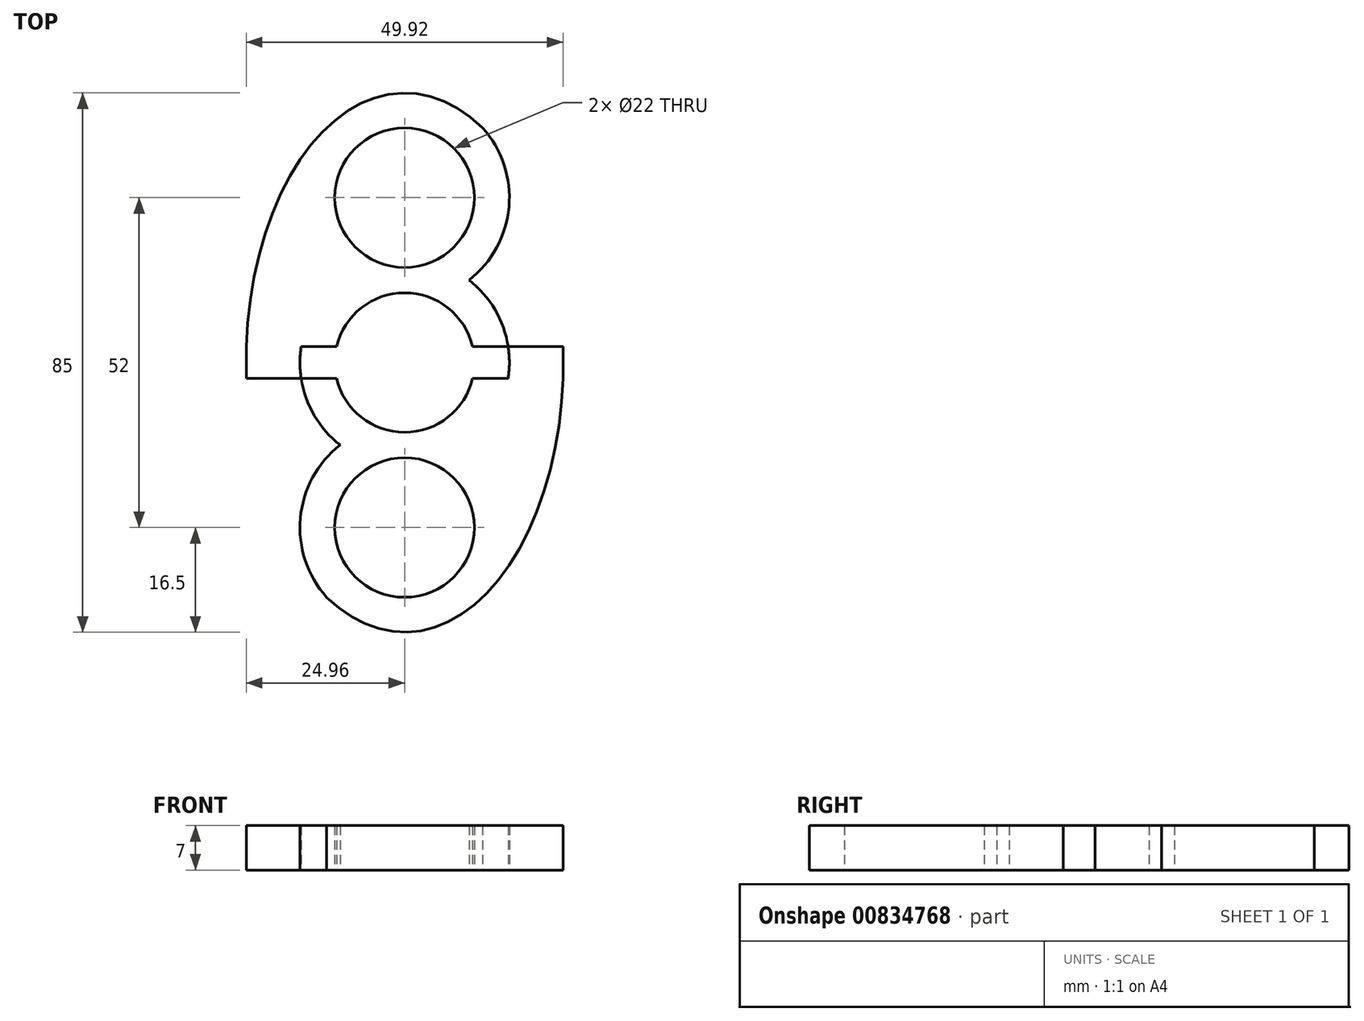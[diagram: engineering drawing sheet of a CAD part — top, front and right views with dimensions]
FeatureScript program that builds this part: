
annotation { "Feature Type Name" : "Feature", "Feature Type Description" : "" }
export const myFeature = defineFeature(function(context is Context, id is Id, definition is map)
    precondition{}
    {
        {
            var Q0;
            Q0=qCreatedBy(makeId("Top.planeOp"),FACE);
            var sketch = newSketch(context, id + "F0", { "sketchPlane" : qUnion([Q0])});
            skEllipse(sketch, "E0", {"center": v(0, 0) * mm, "majorRadius": 42.5 * mm, "minorRadius": 25 * mm, "majorAxis": v(0, 1)});
            skLineSegment(sketch, "E1", {"start": v(0, 0) * mm, "end": v(0, 26) * mm});
            skLineSegment(sketch, "E2.MirrorCS", {"start": v(0, 0) * mm, "end": v(0, -26) * mm});
            skCircle(sketch, "E3", {"center": v(0, 26) * mm, "radius": 11 * mm});
            skCircle(sketch, "E4", {"center": v(0, 0) * mm, "radius": 11 * mm});
            skCircle(sketch, "E5", {"center": v(0, -26) * mm, "radius": 11 * mm});
            skFitSpline(sketch, "E6.0", {"points": [v(1.55, 36.91) * mm, v(0, 37.04) * mm, v(-1.55, 36.91) * mm, v(-3.12, 36.52) * mm, v(-4.74, 35.83) * mm, v(-6.4, 34.82) * mm, v(-8.08, 33.48) * mm, v(-9.75, 31.78) * mm, v(-11.12, 30.07) * mm, v(-12.17, 28.52) * mm, v(-12.94, 27.28) * mm, v(-13.68, 25.95) * mm, v(-14.63, 24.1) * mm, v(-15.7, 21.6) * mm, v(-16.84, 18.4) * mm, v(-17.79, 14.99) * mm, v(-18.54, 11.41) * mm, v(-19.09, 7.7) * mm, v(-19.37, 4.53) * mm, v(-19.48, 1.95) * mm, v(-19.5, 0) * mm, v(-19.48, -1.95) * mm, v(-19.37, -4.53) * mm, v(-19.09, -7.7) * mm, v(-18.54, -11.41) * mm, v(-17.79, -14.99) * mm, v(-16.84, -18.4) * mm, v(-15.7, -21.6) * mm, v(-14.63, -24.1) * mm, v(-13.68, -25.95) * mm, v(-12.94, -27.28) * mm, v(-12.17, -28.52) * mm, v(-11.12, -30.07) * mm, v(-9.75, -31.78) * mm, v(-8.08, -33.48) * mm, v(-6.4, -34.82) * mm, v(-4.74, -35.83) * mm, v(-3.12, -36.52) * mm, v(-1.55, -36.91) * mm, v(0, -37.04) * mm, v(1.55, -36.91) * mm, v(3.12, -36.52) * mm, v(4.74, -35.83) * mm, v(6.4, -34.82) * mm, v(8.08, -33.48) * mm, v(9.75, -31.78) * mm, v(11.12, -30.07) * mm, v(12.17, -28.52) * mm, v(12.94, -27.28) * mm, v(13.68, -25.95) * mm, v(14.63, -24.1) * mm, v(15.7, -21.6) * mm, v(16.84, -18.4) * mm, v(17.79, -14.99) * mm, v(18.54, -11.41) * mm, v(19.09, -7.7) * mm, v(19.37, -4.53) * mm, v(19.48, -1.95) * mm, v(19.5, 0) * mm, v(19.48, 1.95) * mm, v(19.37, 4.53) * mm, v(19.09, 7.7) * mm, v(18.54, 11.41) * mm, v(17.79, 14.99) * mm, v(16.84, 18.4) * mm, v(15.7, 21.6) * mm, v(14.63, 24.1) * mm, v(13.68, 25.95) * mm, v(12.94, 27.28) * mm, v(12.17, 28.52) * mm, v(11.12, 30.07) * mm, v(9.75, 31.78) * mm, v(8.08, 33.48) * mm, v(6.4, 34.82) * mm, v(4.74, 35.83) * mm, v(3.12, 36.52) * mm, v(1.55, 36.91) * mm, v(0, 37.04) * mm, v(-1.55, 36.91) * mm, v(1.55, 36.91) * mm]});
            skCircle(sketch, "E7.0", {"center": v(0, -26) * mm, "radius": 16.5 * mm});
            skCircle(sketch, "E8.0", {"center": v(0, 0) * mm, "radius": 16.5 * mm});
            skCircle(sketch, "E9.0", {"center": v(0, 26) * mm, "radius": 16.5 * mm});
            skLineSegment(sketch, "E10.bottom", {"start": v(-24.96, 2.5) * mm, "end": v(24.96, 2.5) * mm});
            skLineSegment(sketch, "E10.top", {"start": v(-24.96, -2.5) * mm, "end": v(24.96, -2.5) * mm});
            skLineSegment(sketch, "E10.left", {"start": v(-24.96, 2.5) * mm, "end": v(-24.96, -2.5) * mm});
            skLineSegment(sketch, "E10.right", {"start": v(24.96, 2.5) * mm, "end": v(24.96, -2.5) * mm});
            skSolve(sketch);
        }
        {
            var Q0;
            {var subQ5=sQuery(id+"F0.wireOp",EDGE,"E4");var subQ6=sQuery(id+"F0.wireOp",EDGE,"E1");var subQ7=makeQuery(id+"F0.imprint","INTERSECT",VERTEX,{"derivedFrom":[subQ6,subQ5]});Q0=makeQuery(id+"F0.imprint","IMPRINT",FACE,{"disambiguationData":[TD([[makeQuery(id+"F0.imprint","IMPRINT",EDGE,{"disambiguationData":[TD([[subQ7,-1.0]])],"derivedFrom":subQ6}),-1.0]])]});}
            var Q1;
            {var subQ5=sQuery(id+"F0.wireOp",EDGE,"E4");var subQ7=sQuery(id+"F0.wireOp",EDGE,"E1");var subQ8=makeQuery(id+"F0.imprint","INTERSECT",VERTEX,{"derivedFrom":[subQ7,subQ5]});Q1=makeQuery(id+"F0.imprint","IMPRINT",FACE,{"disambiguationData":[TD([[makeQuery(id+"F0.imprint","IMPRINT",EDGE,{"disambiguationData":[TD([[subQ8,-1.0]])],"derivedFrom":subQ7}),1.0]])]});}
            var Q2;
            {var subQ0=sQuery(id+"F0.wireOp",EDGE,"E6.0");var subQ1=sQuery(id+"F0.wireOp",EDGE,"E3");var subQ2=makeQuery(id+"F0.imprint","INTERSECT",VERTEX,{"disambiguationData":[OD(2.0)],"derivedFrom":[subQ1,subQ0]});Q2=makeQuery(id+"F0.imprint","IMPRINT",FACE,{"disambiguationData":[TD([[makeQuery(id+"F0.imprint","IMPRINT",EDGE,{"disambiguationData":[TD([[subQ2,-1.0]])],"derivedFrom":subQ1}),-1.0]])]});}
            var Q3;
            {var subQ5=sQuery(id+"F0.wireOp",EDGE,"E9.0");var subQ6=sQuery(id+"F0.wireOp",EDGE,"E0");var subQ10=makeQuery(id+"F0.imprint","INTERSECT",VERTEX,{"disambiguationData":[OD(0.0)],"derivedFrom":[subQ6,subQ5]});Q3=makeQuery(id+"F0.imprint","IMPRINT",FACE,{"disambiguationData":[TD([[makeQuery(id+"F0.imprint","IMPRINT",EDGE,{"disambiguationData":[TD([[subQ10,1.0]])],"derivedFrom":subQ6}),1.0]])]});}
            var Q4;
            {var subQ0=sQuery(id+"F0.wireOp",EDGE,"E6.0");var subQ1=sQuery(id+"F0.wireOp",EDGE,"E3");var subQ2=makeQuery(id+"F0.imprint","INTERSECT",VERTEX,{"disambiguationData":[OD(1.0)],"derivedFrom":[subQ1,subQ0]});Q4=makeQuery(id+"F0.imprint","IMPRINT",FACE,{"disambiguationData":[TD([[makeQuery(id+"F0.imprint","IMPRINT",EDGE,{"disambiguationData":[TD([[subQ2,1.0]])],"derivedFrom":subQ1}),-1.0]])]});}
            var Q5;
            {var subQ0=sQuery(id+"F0.wireOp",EDGE,"E9.0");var subQ1=sQuery(id+"F0.wireOp",EDGE,"E4");var subQ2=makeQuery(id+"F0.imprint","INTERSECT",VERTEX,{"disambiguationData":[OD(1.0)],"derivedFrom":[subQ1,subQ0]});Q5=makeQuery(id+"F0.imprint","IMPRINT",FACE,{"disambiguationData":[TD([[makeQuery(id+"F0.imprint","IMPRINT",EDGE,{"disambiguationData":[TD([[subQ2,-1.0]])],"derivedFrom":subQ1}),-1.0]])]});}
            var Q6;
            {var subQ0=sQuery(id+"F0.wireOp",EDGE,"E9.0");var subQ1=sQuery(id+"F0.wireOp",EDGE,"E4");var subQ2=makeQuery(id+"F0.imprint","INTERSECT",VERTEX,{"disambiguationData":[OD(0.0)],"derivedFrom":[subQ1,subQ0]});Q6=makeQuery(id+"F0.imprint","IMPRINT",FACE,{"disambiguationData":[TD([[makeQuery(id+"F0.imprint","IMPRINT",EDGE,{"disambiguationData":[TD([[subQ2,1.0]])],"derivedFrom":subQ1}),-1.0]])]});}
            var Q7;
            {var subQ0=sQuery(id+"F0.wireOp",EDGE,"E7.0");var subQ1=sQuery(id+"F0.wireOp",EDGE,"E0");var subQ2=makeQuery(id+"F0.imprint","INTERSECT",VERTEX,{"disambiguationData":[OD(2.0)],"derivedFrom":[subQ1,subQ0]});Q7=makeQuery(id+"F0.imprint","IMPRINT",FACE,{"disambiguationData":[TD([[makeQuery(id+"F0.imprint","IMPRINT",EDGE,{"disambiguationData":[TD([[subQ2,-1.0]])],"derivedFrom":subQ1}),1.0]])]});}
            var Q8;
            {var subQ0=sQuery(id+"F0.wireOp",EDGE,"E9.0");var subQ1=sQuery(id+"F0.wireOp",EDGE,"E0");var subQ2=makeQuery(id+"F0.imprint","INTERSECT",VERTEX,{"disambiguationData":[OD(0.0)],"derivedFrom":[subQ1,subQ0]});Q8=makeQuery(id+"F0.imprint","IMPRINT",FACE,{"disambiguationData":[TD([[makeQuery(id+"F0.imprint","IMPRINT",EDGE,{"disambiguationData":[TD([[subQ2,-1.0]])],"derivedFrom":subQ1}),1.0]])]});}
            var Q9;
            {var subQ0=sQuery(id+"F0.wireOp",EDGE,"E8.0");var subQ1=sQuery(id+"F0.wireOp",EDGE,"E5");var subQ2=makeQuery(id+"F0.imprint","INTERSECT",VERTEX,{"disambiguationData":[OD(1.0)],"derivedFrom":[subQ1,subQ0]});Q9=makeQuery(id+"F0.imprint","IMPRINT",FACE,{"disambiguationData":[TD([[makeQuery(id+"F0.imprint","IMPRINT",EDGE,{"disambiguationData":[TD([[subQ2,-1.0]])],"derivedFrom":subQ1}),-1.0]])]});}
            var Q10;
            {var subQ1=sQuery(id+"F0.wireOp",EDGE,"E4");var subQ7=sQuery(id+"F0.wireOp",EDGE,"E2.MirrorCS");var subQ8=makeQuery(id+"F0.imprint","INTERSECT",VERTEX,{"derivedFrom":[subQ7,subQ1]});Q10=makeQuery(id+"F0.imprint","IMPRINT",FACE,{"disambiguationData":[TD([[makeQuery(id+"F0.imprint","IMPRINT",EDGE,{"disambiguationData":[TD([[subQ8,-1.0]])],"derivedFrom":subQ7}),-1.0]])]});}
            var Q11;
            {var subQ1=sQuery(id+"F0.wireOp",EDGE,"E4");var subQ6=sQuery(id+"F0.wireOp",EDGE,"E2.MirrorCS");var subQ9=makeQuery(id+"F0.imprint","INTERSECT",VERTEX,{"derivedFrom":[subQ6,subQ1]});Q11=makeQuery(id+"F0.imprint","IMPRINT",FACE,{"disambiguationData":[TD([[makeQuery(id+"F0.imprint","IMPRINT",EDGE,{"disambiguationData":[TD([[subQ9,-1.0]])],"derivedFrom":subQ6}),1.0]])]});}
            var Q12;
            {var subQ0=sQuery(id+"F0.wireOp",EDGE,"E8.0");var subQ1=sQuery(id+"F0.wireOp",EDGE,"E5");var subQ2=makeQuery(id+"F0.imprint","INTERSECT",VERTEX,{"disambiguationData":[OD(0.0)],"derivedFrom":[subQ1,subQ0]});Q12=makeQuery(id+"F0.imprint","IMPRINT",FACE,{"disambiguationData":[TD([[makeQuery(id+"F0.imprint","IMPRINT",EDGE,{"disambiguationData":[TD([[subQ2,1.0]])],"derivedFrom":subQ1}),-1.0]])]});}
            var Q13;
            {var subQ5=sQuery(id+"F0.wireOp",EDGE,"E7.0");var subQ6=sQuery(id+"F0.wireOp",EDGE,"E0");var subQ10=makeQuery(id+"F0.imprint","INTERSECT",VERTEX,{"disambiguationData":[OD(0.0)],"derivedFrom":[subQ6,subQ5]});Q13=makeQuery(id+"F0.imprint","IMPRINT",FACE,{"disambiguationData":[TD([[makeQuery(id+"F0.imprint","IMPRINT",EDGE,{"disambiguationData":[TD([[subQ10,-1.0]])],"derivedFrom":subQ6}),1.0]])]});}
            var Q14;
            {var subQ0=sQuery(id+"F0.wireOp",EDGE,"E10.top");var subQ1=sQuery(id+"F0.wireOp",EDGE,"E6.0");var subQ2=makeQuery(id+"F0.imprint","INTERSECT",VERTEX,{"disambiguationData":[OD(1.0)],"derivedFrom":[subQ1,subQ0]});Q14=makeQuery(id+"F0.imprint","IMPRINT",FACE,{"disambiguationData":[TD([[makeQuery(id+"F0.imprint","IMPRINT",EDGE,{"disambiguationData":[TD([[subQ2,-1.0]])],"derivedFrom":subQ1}),1.0]])]});}
            var Q15;
            {var subQ5=sQuery(id+"F0.wireOp",EDGE,"E10.right");Q15=makeQuery(id+"F0.imprint","IMPRINT",FACE,{"disambiguationData":[TD([[makeQuery(id+"F0.imprint","IMPRINT",EDGE,{"derivedFrom":subQ5}),-1.0]])]});}
            var Q16;
            {var subQ0=sQuery(id+"F0.wireOp",EDGE,"E10.bottom");var subQ5=sQuery(id+"F0.wireOp",EDGE,"E6.0");var subQ6=makeQuery(id+"F0.imprint","INTERSECT",VERTEX,{"disambiguationData":[OD(1.0)],"derivedFrom":[subQ5,subQ0]});Q16=makeQuery(id+"F0.imprint","IMPRINT",FACE,{"disambiguationData":[TD([[makeQuery(id+"F0.imprint","IMPRINT",EDGE,{"disambiguationData":[TD([[subQ6,-1.0]])],"derivedFrom":subQ5}),-1.0]])]});}
            var Q17;
            {var subQ0=sQuery(id+"F0.wireOp",EDGE,"E10.bottom");var subQ1=sQuery(id+"F0.wireOp",EDGE,"E4");var subQ2=makeQuery(id+"F0.imprint","INTERSECT",VERTEX,{"disambiguationData":[OD(0.0)],"derivedFrom":[subQ1,subQ0]});Q17=makeQuery(id+"F0.imprint","IMPRINT",FACE,{"disambiguationData":[TD([[makeQuery(id+"F0.imprint","IMPRINT",EDGE,{"disambiguationData":[TD([[subQ2,1.0]])],"derivedFrom":subQ1}),-1.0]])]});}
            var Q18;
            {var subQ0=sQuery(id+"F0.wireOp",EDGE,"E7.0");var subQ1=sQuery(id+"F0.wireOp",EDGE,"E4");var subQ2=makeQuery(id+"F0.imprint","INTERSECT",VERTEX,{"disambiguationData":[OD(1.0)],"derivedFrom":[subQ1,subQ0]});Q18=makeQuery(id+"F0.imprint","IMPRINT",FACE,{"disambiguationData":[TD([[makeQuery(id+"F0.imprint","IMPRINT",EDGE,{"disambiguationData":[TD([[subQ2,-1.0]])],"derivedFrom":subQ1}),-1.0]])]});}
            var Q19;
            {var subQ0=sQuery(id+"F0.wireOp",EDGE,"E10.top");var subQ1=sQuery(id+"F0.wireOp",EDGE,"E4");var subQ2=makeQuery(id+"F0.imprint","INTERSECT",VERTEX,{"disambiguationData":[OD(0.0)],"derivedFrom":[subQ1,subQ0]});Q19=makeQuery(id+"F0.imprint","IMPRINT",FACE,{"disambiguationData":[TD([[makeQuery(id+"F0.imprint","IMPRINT",EDGE,{"disambiguationData":[TD([[subQ2,-1.0]])],"derivedFrom":subQ1}),-1.0]])]});}
            var Q20;
            {var subQ0=sQuery(id+"F0.wireOp",EDGE,"E10.top");var subQ5=sQuery(id+"F0.wireOp",EDGE,"E6.0");var subQ6=makeQuery(id+"F0.imprint","INTERSECT",VERTEX,{"disambiguationData":[OD(0.0)],"derivedFrom":[subQ5,subQ0]});Q20=makeQuery(id+"F0.imprint","IMPRINT",FACE,{"disambiguationData":[TD([[makeQuery(id+"F0.imprint","IMPRINT",EDGE,{"disambiguationData":[TD([[subQ6,-1.0]])],"derivedFrom":subQ5}),-1.0]])]});}
            var Q21;
            {var subQ5=sQuery(id+"F0.wireOp",EDGE,"E10.left");Q21=makeQuery(id+"F0.imprint","IMPRINT",FACE,{"disambiguationData":[TD([[makeQuery(id+"F0.imprint","IMPRINT",EDGE,{"derivedFrom":subQ5}),1.0]])]});}
            var Q22;
            {var subQ0=sQuery(id+"F0.wireOp",EDGE,"E10.bottom");var subQ1=sQuery(id+"F0.wireOp",EDGE,"E6.0");var subQ2=makeQuery(id+"F0.imprint","INTERSECT",VERTEX,{"disambiguationData":[OD(0.0)],"derivedFrom":[subQ1,subQ0]});Q22=makeQuery(id+"F0.imprint","IMPRINT",FACE,{"disambiguationData":[TD([[makeQuery(id+"F0.imprint","IMPRINT",EDGE,{"disambiguationData":[TD([[subQ2,-1.0]])],"derivedFrom":subQ1}),1.0]])]});}
            var Q23;
            {var subQ0=sQuery(id+"F0.wireOp",EDGE,"E10.bottom");var subQ1=sQuery(id+"F0.wireOp",EDGE,"E4");var subQ2=makeQuery(id+"F0.imprint","INTERSECT",VERTEX,{"disambiguationData":[OD(1.0)],"derivedFrom":[subQ1,subQ0]});Q23=makeQuery(id+"F0.imprint","IMPRINT",FACE,{"disambiguationData":[TD([[makeQuery(id+"F0.imprint","IMPRINT",EDGE,{"disambiguationData":[TD([[subQ2,-1.0]])],"derivedFrom":subQ1}),-1.0]])]});}
            extrude(context, id + "F1", {"entities" : qUnion([Q0, Q1, Q2, Q3, Q4, Q5, Q6, Q7, Q8, Q9, Q10, Q11, Q12, Q13, Q14, Q15, Q16, Q17, Q18, Q19, Q20, Q21, Q22, Q23]), "depth" : 7 * mm, "offsetDistance" : 25 * mm});
        }
    });
